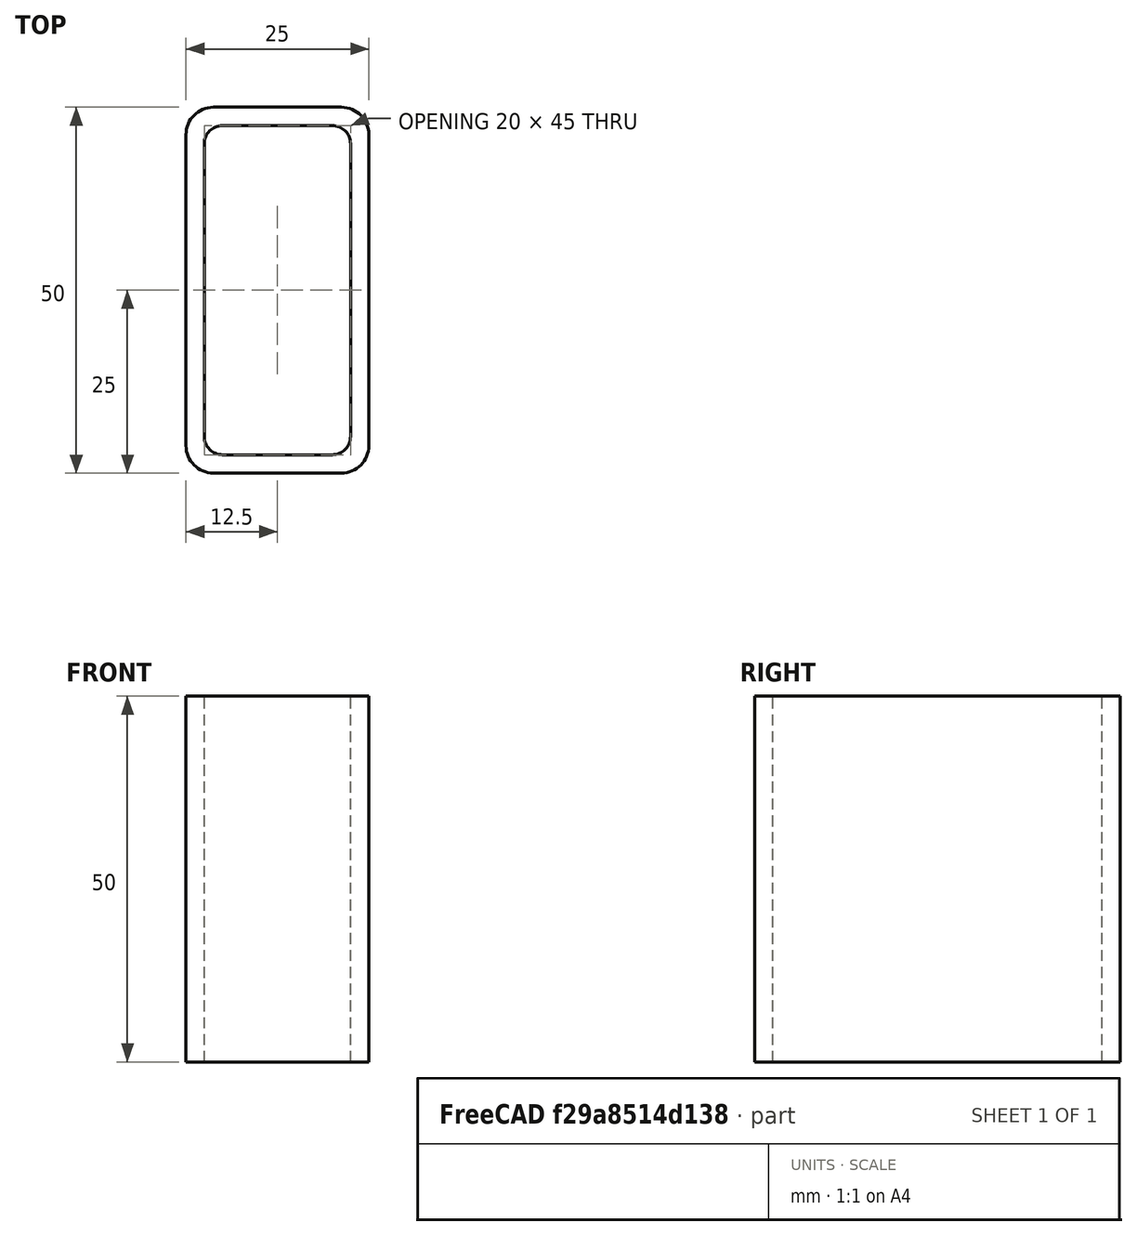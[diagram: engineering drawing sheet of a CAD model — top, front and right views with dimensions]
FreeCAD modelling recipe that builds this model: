
FCSTD DOCUMENT  (FreeCAD 0.15R4671 (Git))
Label: Rectangular hollow section 50x25x2.5 EN10219 S235JRH
License: All rights reserved
LicenseURL: http://en.wikipedia.org/wiki/All_rights_reserved
objects: Sketcher::SketchObject×1, Part::Extrusion×1
note: 2 computed .brp shape members not serialized (recipe doc carries the construction recipe); baked Part::Feature solids carry a one-line shape summary decoded from their .brp

FEATURE [Sketcher::SketchObject] Sketch
  sketch-geometry (16):
    g0: LineSegment StartX=-7.5 StartY=22.5 StartZ=0 EndX=7.5 EndY=22.5 EndZ=0
    g1: LineSegment StartX=10 StartY=20 StartZ=0 EndX=10 EndY=-20 EndZ=0
    g2: LineSegment StartX=7.5 StartY=-22.5 StartZ=0 EndX=-7.5 EndY=-22.5 EndZ=0
    g3: LineSegment StartX=-10 StartY=-20 StartZ=0 EndX=-10 EndY=20 EndZ=0
    g4: LineSegment StartX=-8.75 StartY=25 StartZ=0 EndX=8.75 EndY=25 EndZ=0
    g5: LineSegment StartX=12.5 StartY=21.25 StartZ=0 EndX=12.5 EndY=-21.25 EndZ=0
    g6: LineSegment StartX=8.75 StartY=-25 StartZ=0 EndX=-8.75 EndY=-25 EndZ=0
    g7: LineSegment StartX=-12.5 StartY=-21.25 StartZ=0 EndX=-12.5 EndY=21.25 EndZ=0
    g8: ArcOfCircle CenterX=-7.5 CenterY=20 CenterZ=0 NormalX=0 NormalY=0 NormalZ=1 Radius=2.5 StartAngle=1.5708 EndAngle=3.14159
    g9: ArcOfCircle CenterX=7.5 CenterY=20 CenterZ=0 NormalX=0 NormalY=0 NormalZ=1 Radius=2.5 StartAngle=0 EndAngle=1.5708
    g10: ArcOfCircle CenterX=7.5 CenterY=-20 CenterZ=0 NormalX=0 NormalY=0 NormalZ=1 Radius=2.5 StartAngle=4.71239 EndAngle=6.28319
    g11: ArcOfCircle CenterX=-7.5 CenterY=-20 CenterZ=0 NormalX=0 NormalY=0 NormalZ=1 Radius=2.5 StartAngle=3.14159 EndAngle=4.71239
    g12: ArcOfCircle CenterX=8.75 CenterY=21.25 CenterZ=0 NormalX=0 NormalY=0 NormalZ=1 Radius=3.75 StartAngle=0 EndAngle=1.5708
    g13: ArcOfCircle CenterX=8.75 CenterY=-21.25 CenterZ=0 NormalX=0 NormalY=0 NormalZ=1 Radius=3.75 StartAngle=4.71239 EndAngle=6.28319
    g14: ArcOfCircle CenterX=-8.75 CenterY=-21.25 CenterZ=0 NormalX=0 NormalY=0 NormalZ=1 Radius=3.75 StartAngle=3.14159 EndAngle=4.71239
    g15: ArcOfCircle CenterX=-8.75 CenterY=21.25 CenterZ=0 NormalX=0 NormalY=0 NormalZ=1 Radius=3.75 StartAngle=1.5708 EndAngle=3.14159
  constraints (36):
    c: Horizontal(g2)
    c: Vertical(g3)
    c: Horizontal(g6)
    c: Vertical(g7)
    c: Tangent(g3,g8) = 1.5708
    c: Tangent(g0,g8) = 1.5708
    c: Tangent(g0,g9) = 1.5708
    c: Tangent(g1,g9) = 1.5708
    c: Tangent(g1,g10) = 1.5708
    c: Tangent(g2,g10) = 1.5708
    c: Tangent(g2,g11) = 1.5708
    c: Tangent(g3,g11) = 1.5708
    c: Tangent(g4,g12) = 1.5708
    c: Tangent(g5,g12) = 1.5708
    c: Tangent(g5,g13) = 1.5708
    c: Tangent(g6,g13) = 1.5708
    c: Tangent(g6,g14) = 1.5708
    c: Tangent(g7,g14) = 1.5708
    c: Tangent(g7,g15) = 1.5708
    c: Tangent(g4,g15) = 1.5708
    c: Equal(g9,g8)
    c: Equal(g9,g11)
    c: Equal(g9,g10)
    c: Equal(g12,g15)
    c: Equal(g12,g14)
    c: Equal(g12,g13)
    c: Symmetric(g4,g6,g-1)
    c: Symmetric(g7,g5,g-2)
    c: DistanceY(g4,g6) = -50
    c: DistanceX(g7,g5) = 25
    c: Symmetric(g3,g1,g-2)
    c: Symmetric(g0,g2,g-1)
    c: DistanceY(g0,g4) = 2.5
    c: DistanceX(g5,g1) = -2.5
    c: Radius(g9) = 2.5
    c: Radius(g12) = 3.75
FEATURE [Part::Extrusion] Extrude  label="Rectangular hollow section 50x25x2.5 EN10219 S235JRH"
  Base = -> Sketch
  Dir = (0,0,50)
  Solid = true
